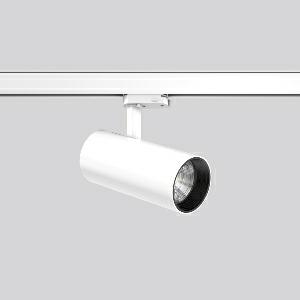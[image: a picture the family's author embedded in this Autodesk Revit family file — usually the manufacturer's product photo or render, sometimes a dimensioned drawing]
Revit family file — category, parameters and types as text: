
# Revit family: deecos_s_mini_742198_002_3_76_0ad7
name_source: partatom
category: Lighting Fixtures
units: mm (PartAtom-declared; Revit-internal decimal feet)

## family parameters
Cut with Voids When Loaded = No
Host = Face
Light Source = No
Part Type = Normal
Room Calculation Point = No
Round Connector Dimension = Use Diameter
Shared = No

## types (1)
- DEECOS S mini (1 x LED Modul 935, 2250 lm, 3500)
    Apparent Load = 20 VA
    Approval mark = CE
    CIE Flux Codes = 99 100 100 100 100
    Color Rendering = 92
    Color Temperature = 3500
    Default Elevation = 1800 mm
    Description = Series: DEECOS S mini
LED surface-mounted projector in modern design with no visible cooling ribs. Housing: die-cast aluminium, powder-coated. Rotation range: 356°. Swivel range: 90°. Black plastic ring and recessed LED to prevent glare from the side. Optical assembly with lens made of plastic (polycarbonate) for the best homogeneous light distribution - can be changed without tools. Best colour rendering index Ra>90. With adapter for RZB 3-circuit DALI tracks. Suitable for Track on ceiling, Wall track. High quality converter without flickering and stroboscopic effect. The following accessories can be mounted without use of tools: interchangeable lenses, decorative glasses, honeycomb louvre, clear and frosted diffusers, white interchangeable plastic ring. 
Colour: traffic white, matt (RAL 9016)
Diameter: 87 mm
Height: 214 mm
Lamp: LED
Socket: without socket
Colour temperature: 3500K
Colour rendering index (CRI): 92
System power: 20 W
Rated luminous flux: 2250 lm
Luminous efficiency: 113 lm/W
Control gear: Converter, dimmable, DALI
Protection class: I
Type of protection: IP 20
    Height = 214 mm
    Lamp = 1 x LED Modul 935
    Lamp Light Flux = 2250 lm
    Lamp count = 1
    Length = 87 mm
    Lifetime = 50000 h
    Luminous efficacy = 113 lm/W
    Manufacturer = RZB
    ModVariant = No
    Model = 742198.002.3.76
    Mounting Place = Ceiling
    Mounting Type = Rail mounted
    Number of Poles = 1
    OnlyDefault = Yes
    Power Factor = 1
    Product Name = DEECOS S mini
    Product group = Track mounted projectors
    ProductGroupID = 301
    Protection Class = Protection class I
    Protection Degree = IP 20
    RLX_Detail_Level = 1
    RLX_Emergency_Light_Flux = 0 lm
    RLX_Emergency_Type = 0
    RLX_Emergency_Type_DB = No
    RlxData = <blob elided: 35345 chars, md5=632adeaf>
    Socket = socket
    Standby Power = 0 W
    System Light Flux = 2250 lm
    System Power = 20 W
    Type Comments = Product without accessories
    Type Image = 741930.002.jpg
    URL = http://relux.com
    VarID = ---
    Voltage = 230 V
    Voltage Range = 220-240 V
    Weight = 0.00 kg
    Width = 0 mm  [stored 0 ft]

note: [stored X ft] marks values corroborated as IEEE doubles in the binary element streams (Revit-internal decimal feet)

## geometry (parser evidence)
native form markers: Blend x4, Sweep x13
no freeform markers — native parametric forms only
